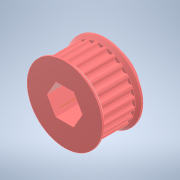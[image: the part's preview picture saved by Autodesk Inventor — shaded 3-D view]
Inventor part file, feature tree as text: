
AUTODESK INVENTOR PART (.ipt)
format: ipt  version: 2022.3 (Build 263350000, 350)  size: 324,608 bytes
history: native  units: in
note: dims shown in document units (in); Inventor stores cm internally (conversion verified against a paired STEP export)
features: extrude x7, sketch x7, mirror x2, chamfer x2, other x1, fillet x1, pattern_circular x1, projected_geometry x1
ambient origin geometry x8: Origin, YZ Plane, XZ Plane, XY Plane, X Axis, Y Axis, Z Axis, Center Point
bodies: Solid1 (feature_tree)
feature tree (22):
  other  "Hex Bore"
  extrude  "HTD Base"  Depth=0.3937in TaperAngle=0.0deg
  extrude  "HTD Flange"  Depth=0.0591in
  mirror  "HTD Flanges"
  chamfer  "HTD Flange Chamfer"  Distance=0.0787in Angle=45.0deg
  extrude  "GT2 Base"  TaperAngle=0.0deg  [1 undecoded]
  extrude  "GT2 Base Tooth"  TaperAngle=0.0deg  [1 undecoded]
  fillet  "GT2 Base Tooth pt. 2"  Radius=0.8723in
  pattern_circular  "GT2 Teeth"  [2 undecoded]
  extrude  "GT2 Flange"  Depth=0.125in
  mirror  "GT2 Flanges"
  chamfer  "GT2 Flange Chamfer"  Distance=0.0075in
  extrude  "Circle Bore"  TaperAngle=0.0deg  [1 undecoded]
  sketch  "Sketch9"  dims[d25=0.3937in d26=0.0in d27=0.0727in d28=0.0075in d29=0.0in d30=0.0in d31=0.0118in d32=9.4488in d33=360.0deg d35=0.0394in d36=0.0591in d37=0.0in d38=0.0394in d39=0.0787in d40=45.0deg d41=0.625in d42=0.125in d43=0.0in]
  extrude  "Extrusion9"  Depth=0.0118in
  sketch  "Sketch1"  dims[d0=1.4588in d1=0.3937in d2=0.0in]
  sketch  "Sketch4"  dims[d12=0.0394in d13=0.0591in]
  sketch  "Sketch5"  dims[d14=0.0in]
  sketch  "Sketch6"  dims[d15=0.0394in d16=0.0787in d17=45.0deg]
  sketch  "Sketch7"  dims[d18=0.385in d19=0.0in d20=0.0in]
  sketch  "Sketch8"  dims[d21=0.385in d22=0.0in d23=0.0in d24=0.8723in]
  projected_geometry  "Projected Loop1"
note: 5 required parameter values undecoded (feature->parameter linkage not recoverable at this tier; creation-order binding heuristic only, values carry confidence <= 0.55)
